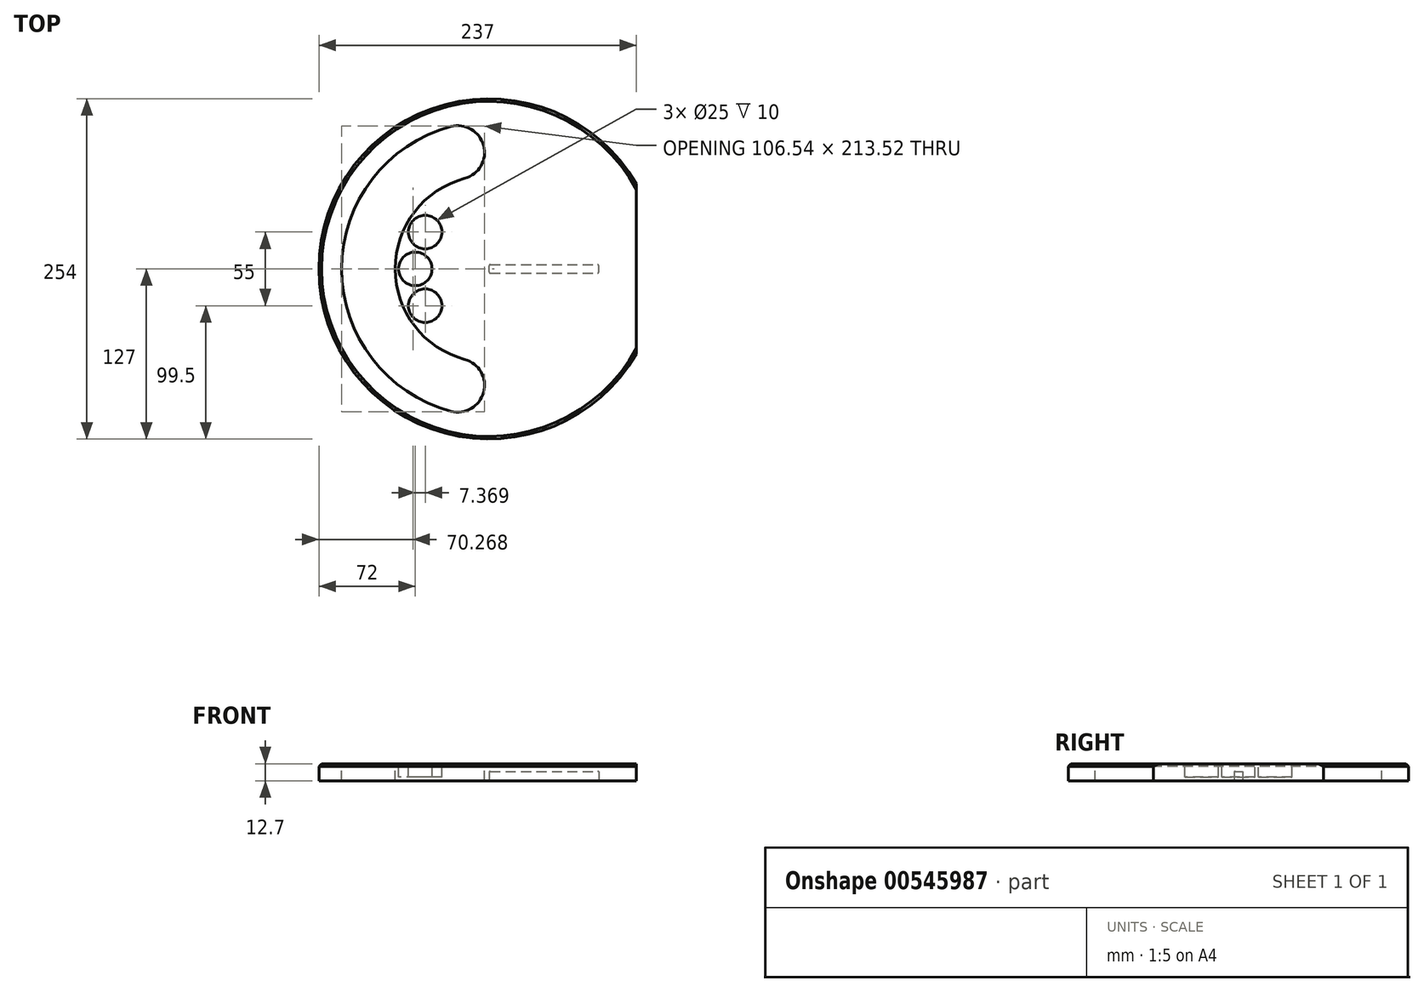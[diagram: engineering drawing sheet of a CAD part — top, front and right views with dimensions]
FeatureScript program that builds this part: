
annotation { "Feature Type Name" : "Feature", "Feature Type Description" : "" }
export const myFeature = defineFeature(function(context is Context, id is Id, definition is map)
    precondition{}
    {
        {
            var Q0;
            Q0=qCreatedBy(makeId("Top.planeOp"),FACE);
            var sketch = newSketch(context, id + "F0", { "sketchPlane" : qUnion([Q0])});
            skCircle(sketch, "E0", {"center": v(0, 0) * mm, "radius": 127 * mm});
            skSolve(sketch);
        }
        {
            var Q0;
            Q0 = qSketchRegion(id + "F0", true);
            extrude(context, id + "F1", {"entities" : qUnion([Q0]), "endBound" : BoundingType.SYMMETRIC, "depth" : 12.7 * mm, "offsetDistance" : 25 * mm});
        }
        {
            var Q0;
            Q0=makeQuery(id+"F1.opExtrude","CAP_FACE",FACE,{"disambiguationData":[OSD([sQuery(id+"F0.wireOp",EDGE,"E0")])],"isStart":false});
            var sketch = newSketch(context, id + "F2", { "sketchPlane" : qUnion([Q0])});
            skSolve(sketch);
        }
        {
            var Q0;
            Q0=makeQuery(id+"F2.imprint","IMPRINT",FACE,{"disambiguationData":[TD([[makeQuery(id+"F2.imprint","IMPRINT",EDGE,{"derivedFrom":makeQuery(id+"F1.opExtrude","CAP_EDGE",EDGE,{"disambiguationData":[OSD([sQuery(id+"F0.wireOp",EDGE,"E0")])],"isStart":false})}),1.0]])]});
            var sketch = newSketch(context, id + "F3", { "sketchPlane" : qUnion([Q0])});
            skArc(sketch, "E1", {"start": v(-18.12, 67.61) * mm, "mid": v(-70, 0) * mm, "end": v(-18.12, -67.61) * mm});
            skArc(sketch, "E2", {"start": v(-28.47, 106.25) * mm, "mid": v(-110, 0) * mm, "end": v(-28.47, -106.25) * mm});
            skCircle(sketch, "E3", {"center": v(0, 0) * mm, "radius": 90 * mm, "construction": true});
            skLineSegment(sketch, "E4", {"start": v(0, 110) * mm, "end": v(0, 70) * mm, "construction": true});
            skPoint(sketch, "E5", {"position": v(0, 90) * mm});
            skLineSegment(sketch, "E6", {"start": v(0, 0) * mm, "end": v(-23.3, 86.93) * mm, "construction": true});
            skLineSegment(sketch, "E7", {"start": v(0, 0) * mm, "end": v(-23.3, -86.93) * mm, "construction": true});
            skArc(sketch, "E8", {"start": v(-18.12, 67.61) * mm, "mid": v(-3.98, 92.1) * mm, "end": v(-28.47, 106.25) * mm});
            skArc(sketch, "E9", {"start": v(-28.47, -106.25) * mm, "mid": v(-3.98, -92.1) * mm, "end": v(-18.12, -67.61) * mm});
            skSolve(sketch);
        }
        {
            var Q0;
            Q0 = qSketchRegion(id + "F3", true);
            extrude(context, id + "F4", {"entities" : qUnion([Q0]), "operationType" : NewBodyOperationType.REMOVE, "endBound" : BoundingType.UP_TO_NEXT, "oppositeDirection" : true, "depth" : 25 * mm, "offsetDistance" : 25 * mm});
        }
        {
            var Q0;
            Q0=makeQuery(id+"F2.imprint","IMPRINT",FACE,{"disambiguationData":[TD([[makeQuery(id+"F2.imprint","IMPRINT",EDGE,{"derivedFrom":makeQuery(id+"F1.opExtrude","CAP_EDGE",EDGE,{"disambiguationData":[OSD([sQuery(id+"F0.wireOp",EDGE,"E0")])],"isStart":false})}),1.0]])]});
            var sketch = newSketch(context, id + "F5", { "sketchPlane" : qUnion([Q0])});
            skCircle(sketch, "E10", {"center": v(0, 0) * mm, "radius": 55 * mm, "construction": true});
            skLineSegment(sketch, "E11", {"start": v(-47.63, 27.5) * mm, "end": v(0, 0) * mm, "construction": true});
            skLineSegment(sketch, "E12", {"start": v(-55, 0) * mm, "end": v(0, 0) * mm, "construction": true});
            skLineSegment(sketch, "E13", {"start": v(0, 0) * mm, "end": v(-47.63, -27.5) * mm, "construction": true});
            skCircle(sketch, "E14", {"center": v(-47.63, 27.5) * mm, "radius": 12.5 * mm});
            skCircle(sketch, "E15", {"center": v(-55, 0) * mm, "radius": 12.5 * mm});
            skCircle(sketch, "E16", {"center": v(-47.63, -27.5) * mm, "radius": 12.5 * mm});
            skSolve(sketch);
        }
        {
            var Q0;
            Q0 = qSketchRegion(id + "F5", true);
            extrude(context, id + "F6", {"entities" : qUnion([Q0]), "operationType" : NewBodyOperationType.REMOVE, "oppositeDirection" : true, "depth" : 10 * mm, "offsetDistance" : 25 * mm});
        }
        {
            var Q0;
            Q0=makeQuery(id+"F2.imprint","IMPRINT",FACE,{"disambiguationData":[TD([[makeQuery(id+"F2.imprint","IMPRINT",EDGE,{"derivedFrom":makeQuery(id+"F1.opExtrude","CAP_EDGE",EDGE,{"disambiguationData":[OSD([sQuery(id+"F0.wireOp",EDGE,"E0")])],"isStart":false})}),1.0]])]});
            var sketch = newSketch(context, id + "F7", { "sketchPlane" : qUnion([Q0])});
            skCircle(sketch, "E17", {"center": v(24.02, 0) * mm, "radius": 55 * mm});
            skSolve(sketch);
        }
        {
            var Q0;
            Q0=makeQuery(id+"F4.boolean.opBoolean","COPY",EDGE,{"derivedFrom":makeQuery(id+"F4.opExtrude","CAP_EDGE",EDGE,{"disambiguationData":[OSD([sQuery(id+"F3.wireOp",EDGE,"E2")])],"isStart":true})});
            var Q1;
            Q1=makeQuery(id+"F1.opExtrude","CAP_EDGE",EDGE,{"disambiguationData":[OSD([sQuery(id+"F0.wireOp",EDGE,"E0")])],"isStart":false});
            chamfer(context, id + "F8", {"entities" : qUnion([Q0, Q1]), "width" : 2 * mm, "tangentPropagation" : true});
        }
        {
            var Q0;
            Q0=makeQuery(id+"F7.imprint","IMPRINT",FACE,{"disambiguationData":[TD([[makeQuery(id+"F7.imprint","IMPRINT",EDGE,{"derivedFrom":sQuery(id+"F7.wireOp",EDGE,"E17")}),-1.0]])]});
            var sketch = newSketch(context, id + "F9", { "sketchPlane" : qUnion([Q0])});
            skLineSegment(sketch, "E18.bottom", {"start": v(138.84, 75.55) * mm, "end": v(110, 75.55) * mm});
            skLineSegment(sketch, "E18.top", {"start": v(138.84, -79.57) * mm, "end": v(110, -79.57) * mm});
            skLineSegment(sketch, "E18.left", {"start": v(138.84, 75.55) * mm, "end": v(138.84, -79.57) * mm});
            skLineSegment(sketch, "E18.right", {"start": v(110, 75.55) * mm, "end": v(110, -79.57) * mm});
            skSolve(sketch);
        }
        {
            var Q0;
            Q0 = qSketchRegion(id + "F9", true);
            extrude(context, id + "F10", {"entities" : qUnion([Q0]), "operationType" : NewBodyOperationType.REMOVE, "endBound" : BoundingType.UP_TO_NEXT, "oppositeDirection" : true, "depth" : 25 * mm, "offsetDistance" : 25 * mm});
        }
        {
            var Q0;
            Q0=makeQuery(id+"F1.opExtrude","CAP_FACE",FACE,{"disambiguationData":[OSD([sQuery(id+"F0.wireOp",EDGE,"E0")])],"isStart":true});
            var sketch = newSketch(context, id + "F11", { "sketchPlane" : qUnion([Q0])});
            skLineSegment(sketch, "E19.bottom", {"start": v(0, 3.2) * mm, "end": v(82, 3.2) * mm});
            skLineSegment(sketch, "E19.top", {"start": v(0, -3.2) * mm, "end": v(82, -3.2) * mm});
            skLineSegment(sketch, "E19.left", {"start": v(0, 3.2) * mm, "end": v(0, -3.2) * mm});
            skLineSegment(sketch, "E19.right", {"start": v(82, 3.2) * mm, "end": v(82, -3.2) * mm});
            skSolve(sketch);
        }
        {
            var Q0;
            Q0 = qSketchRegion(id + "F11", true);
            extrude(context, id + "F12", {"entities" : qUnion([Q0]), "operationType" : NewBodyOperationType.REMOVE, "oppositeDirection" : true, "depth" : 7 * mm, "offsetDistance" : 25 * mm});
        }
        {
            var Q0;
            Q0=makeQuery(id+"F12.boolean.opBoolean","COPY",EDGE,{"derivedFrom":makeQuery(id+"F12.opExtrude","SWEPT_EDGE",EDGE,{"disambiguationData":[OSD([sQuery(id+"F11.wireOp",EDGE,"E19.bottom"),sQuery(id+"F11.wireOp",EDGE,"E19.left")])]})});
            var Q1;
            Q1=makeQuery(id+"F12.boolean.opBoolean","COPY",EDGE,{"derivedFrom":makeQuery(id+"F12.opExtrude","SWEPT_EDGE",EDGE,{"disambiguationData":[OSD([sQuery(id+"F11.wireOp",EDGE,"E19.top"),sQuery(id+"F11.wireOp",EDGE,"E19.left")])]})});
            var Q2;
            Q2=makeQuery(id+"F12.boolean.opBoolean","COPY",EDGE,{"derivedFrom":makeQuery(id+"F12.opExtrude","SWEPT_EDGE",EDGE,{"disambiguationData":[OSD([sQuery(id+"F11.wireOp",EDGE,"E19.top"),sQuery(id+"F11.wireOp",EDGE,"E19.right")])]})});
            var Q3;
            Q3=makeQuery(id+"F12.boolean.opBoolean","COPY",EDGE,{"derivedFrom":makeQuery(id+"F12.opExtrude","SWEPT_EDGE",EDGE,{"disambiguationData":[OSD([sQuery(id+"F11.wireOp",EDGE,"E19.bottom"),sQuery(id+"F11.wireOp",EDGE,"E19.right")])]})});
            fillet(context, id + "F13", {"entities" : qUnion([Q0, Q1, Q2, Q3]), "radius" : 1 * mm, "tangentPropagation" : true, "allowEdgeOverflow" : false});
        }
    });
